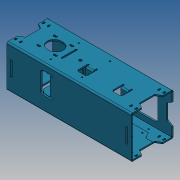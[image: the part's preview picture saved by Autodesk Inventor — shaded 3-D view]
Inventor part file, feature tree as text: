
AUTODESK INVENTOR PART (.ipt)
format: ipt  version: 2017 (Build 210142000, 142)  size: 1,296,384 bytes
history: native  units: mm
features: other x15, sketch x4, extrude x2, mirror x2, projected_geometry x2, plane x1
ambient origin geometry x8: Origin, YZ Plane, XZ Plane, XY Plane, X Axis, Y Axis, Z Axis, Center Point
bodies: Body1 (feature_tree)
feature tree (26):
  other  "Sólido1"
  sketch  "Boceto1"  dims[d1=56.4mm d2=72.0mm]
  extrude  "Extrusión1"  Depth=72.0mm
  other  "Pliegue2"
  other  "Pliegue4"
  sketch  "Boceto4"  dims[d4=200.0mm d5=42.0mm]
  other  "Cara1"
  other  "Pliegue3"
  mirror  "Simetría2"
  sketch  "Boceto5"  dims[d6=8.0mm]
  other  "Cara4"
  other  "Cara5"
  plane  "Plano de trabajo1"
  mirror  "Simetría1"
  other  "Pliegue5"
  extrude  "Extrusión6"  Depth=42.0mm
  other  "Placa2"
  other  "Doblez2"
  projected_geometry  "Contorno proyectado6"
  other  "Placa5"
  other  "Doblez5"
  other  "Placa6"
  other  "Doblez6"
  sketch  "Boceto7"  dims[d8=5.0mm d9=41.14mm d10=6.0mm d11=53.14mm d12=6.0mm d13=4.0mm d14=100.0mm d15=20.0mm d16=80.0mm d17=60.0mm d18=4.0mm d19=33.93mm d20=22.0mm d21=120.0mm d22=130.0mm d23=20.0mm d24=4.0mm d25=0.0mm d42=47.14mm d43=47.14mm d44=20.0mm d45=6.0mm d46=14.2mm d47=25.0mm d48=0.1mm d49=4.0mm d50=2.0mm d51=8.0mm d52=4.0mm d62=4.4mm d63=41.0mm d70=4.4mm d71=130.7mm d86=50.0mm d87=355.0mm d88=12.5mm d89=12.5mm d90=23.6mm d91=11.8mm d97=190.1mm d134=4.0mm d135=2.0mm d136=8.0mm d137=4.0mm d138=90.0deg d139=0.1mm d142=10.0mm d143=4.0mm d144=80.0mm d145=5.0mm d146=60.0deg d155=60.0deg d156=41.0mm d159=60.0deg d160=112.0mm d161=60.0deg d162=2.0mm d163=6.0mm d165=4.0mm d166=33.0mm d168=15.0mm d169=60.0mm d171=30.0mm d172=4.0mm d173=21.0mm d174=10.5mm d175=4.0mm d176=2.0mm d177=8.0mm d178=4.0mm d179=90.0deg d180=0.5mm d181=8.0mm d182=15.0mm d183=4.0mm d184=8.0mm d185=2.0mm d186=21.0mm d187=10.5mm d188=20.0mm d189=8.0mm d190=20.0mm d192=100.0mm d193=10.0mm d195=10.0mm d197=120.0mm d198=4.0mm d199=2.0mm d200=8.0mm d201=4.0mm d202=90.0deg d203=0.1mm d204=25.0mm d205=25.0mm d206=6.0mm d207=58.8mm d209=2.0mm d210=8.0mm d211=10.0mm d212=50.0mm d215=4.0mm d216=18.0mm d217=12.0mm d218=1.0mm d219=21.0mm d220=8.0mm d221=0.1mm d222=1.0mm d224=0.1mm d225=4.2mm d226=12.0mm d227=4.2mm d228=4.2mm d229=50.0mm d230=75.0mm d233=0.1mm d234=3.7mm d237=13.4mm d238=1.0mm d239=0.1mm d240=0.1mm d241=4.0mm d242=2.0mm d243=8.0mm d244=4.0mm d245=0.1mm d246=4.0mm d247=2.0mm d248=8.0mm d249=4.0mm d250=4.0mm d251=2.0mm d252=8.0mm d253=4.0mm d254=90.0deg d255=0.1mm d256=10.0mm d257=0.0mm d258=20.0mm d259=3.0mm d260=4.0mm d261=0.05mm d262=152.0mm d263=18.0mm d264=18.0mm d265=18.0mm d266=22.0mm d267=0.1mm d268=0.1mm d269=120.0deg d270=20.0mm d271=4.0mm]
  projected_geometry  "Contorno proyectado7"
  other  "Definición1"
